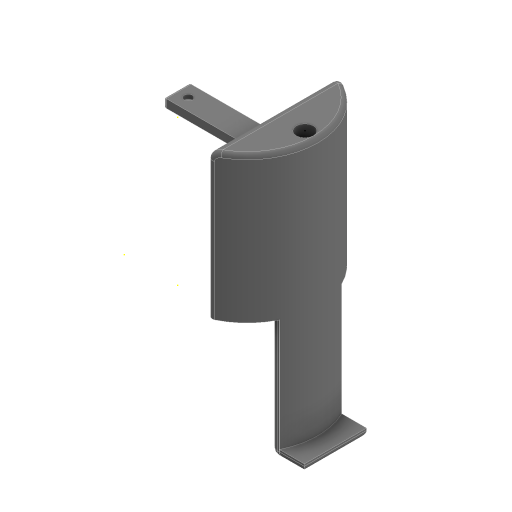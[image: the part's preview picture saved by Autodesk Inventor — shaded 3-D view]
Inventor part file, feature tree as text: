
AUTODESK INVENTOR PART (.ipt)
format: ipt  version: 2023 (Build 270158000, 158)  size: 348,160 bytes
history: native  units: mm
features: sketch x24, extrude x14, fillet x8, other x2, loft x1
ambient origin geometry x8: Origin, YZ Plane, XZ Plane, XY Plane, X Axis, Y Axis, Z Axis, Center Point
bodies: Solid1 (feature_tree)
feature tree (49):
  sketch  "Sketch1"  dims[d2=34.0mm d3=12.0mm]
  sketch  "3D Sketch1"
  extrude  "Extrusion1"  Depth=12.0mm
  sketch  "Sketch6"  dims[d23=15.0mm d24=27.0mm d25=0.0mm]
  sketch  "Sketch7"  dims[d26=6.0mm d27=2.0mm d28=0.0mm]
  sketch  "Sketch8"  dims[d29=2.0mm d30=0.0mm d43=2.0mm]
  extrude  "Extrusion7"  Depth=34.0mm
  sketch  "Sketch12"  dims[d69=6.0mm d70=2.0mm d71=23.0mm d72=0.0mm d73=1.5mm]
  extrude  "Extrusion8"  Depth=27.0mm TaperAngle=0.0deg
  extrude  "Extrusion9"  Depth=2.0mm TaperAngle=0.0deg
  extrude  "Extrusion13"  Depth=2.0mm
  sketch  "Sketch19"  dims[d87=0.5mm d90=4.15mm d91=4.13mm]
  extrude  "Extrusion15"  Depth=1.0mm TaperAngle=0.0deg
  extrude  "Extrusion21"  Depth=2.0mm
  sketch  "Sketch27"  dims[d164=2.0mm d165=2.0mm]
  sketch  "Sketch28"  dims[d166=60.0mm d168=360.0deg d170=8.0mm d171=0.0mm]
  fillet  "Fillet3"  Radius=23.0mm
  fillet  "Fillet4"  Radius=1.5mm
  sketch  "Sketch29"  dims[d172=13.0mm d173=5.0mm]
  extrude  "Extrusion23"  Depth=2.0mm
  fillet  "Fillet6"  Radius=8.0mm
  fillet  "Fillet7"  Radius=3.0mm
  sketch  "Sketch32"  dims[d182=0.0mm d183=90.0deg d185=2.0mm]
  extrude  "Extrusion24"  Depth=4.15mm
  fillet  "Fillet10"  Radius=4.13mm
  sketch  "Sketch39"  dims[d187=2.0mm]
  extrude  "Extrusion29"  Depth=3.0mm
  fillet  "Fillet12"  Radius=18.0mm
  extrude  "Extrusion34"  Depth=9.0mm
  extrude  "Extrusion35"  Depth=2.0mm
  extrude  "Extrusion36"  Depth=8.0mm TaperAngle=0.0deg
  loft  "Loft6"
  fillet  "Fillet13"  Radius=10.0mm
  fillet  "Fillet14"  [1 undecoded]
  extrude  "Extrusion37"  Depth=2.0mm
  sketch  "Sketch2"  dims[d4=35.0mm d5=0.0mm d22=34.0mm]
  sketch  "Sketch11"  dims[d44=0.0mm d45=0.0mm d51=1.0mm d52=0.0mm]
  sketch  "Sketch17"  dims[d74=1.5mm d79=2.0mm d80=8.0mm d81=0.0mm d86=3.0mm]
  sketch  "Sketch21"  dims[d92=12.0mm d93=0.0mm d98=3.0mm d135=18.0mm]
  sketch  "Sketch26"  dims[d136=7.5mm d137=0.0mm d163=9.0mm]
  sketch  "Sketch31"  dims[d174=0.2mm d175=1.2mm d176=0.0mm d177=0.0mm d178=10.0mm d179=0.0mm d180=0.0mm d181=90.0deg]
  sketch  "Sketch33"  dims[d186=1.0mm]
  sketch  "Sketch40"  dims[d188=1.0mm d189=0.0mm]
  sketch  "Sketch45"  dims[d94=0.872665mm]
  sketch  "Sketch46"  dims[d111=0.5mm]
  sketch  "Sketch47"  dims[d112=0.872665mm]
  other  "Edges10"
  other  "Edges11"
  sketch  "Sketch49"  dims[d113=0.5mm d114=0.872665mm d115=0.5mm d116=0.872665mm d117=0.5mm d118=0.872665mm d123=0.5mm d124=0.872665mm d125=0.5mm d126=0.872665mm d150=0.5mm d151=0.872665mm d152=0.5mm d153=0.872665mm d190=0.872665mm]
note: 1 required parameter value undecoded (feature->parameter linkage not recoverable at this tier; creation-order binding heuristic only, values carry confidence <= 0.55)
